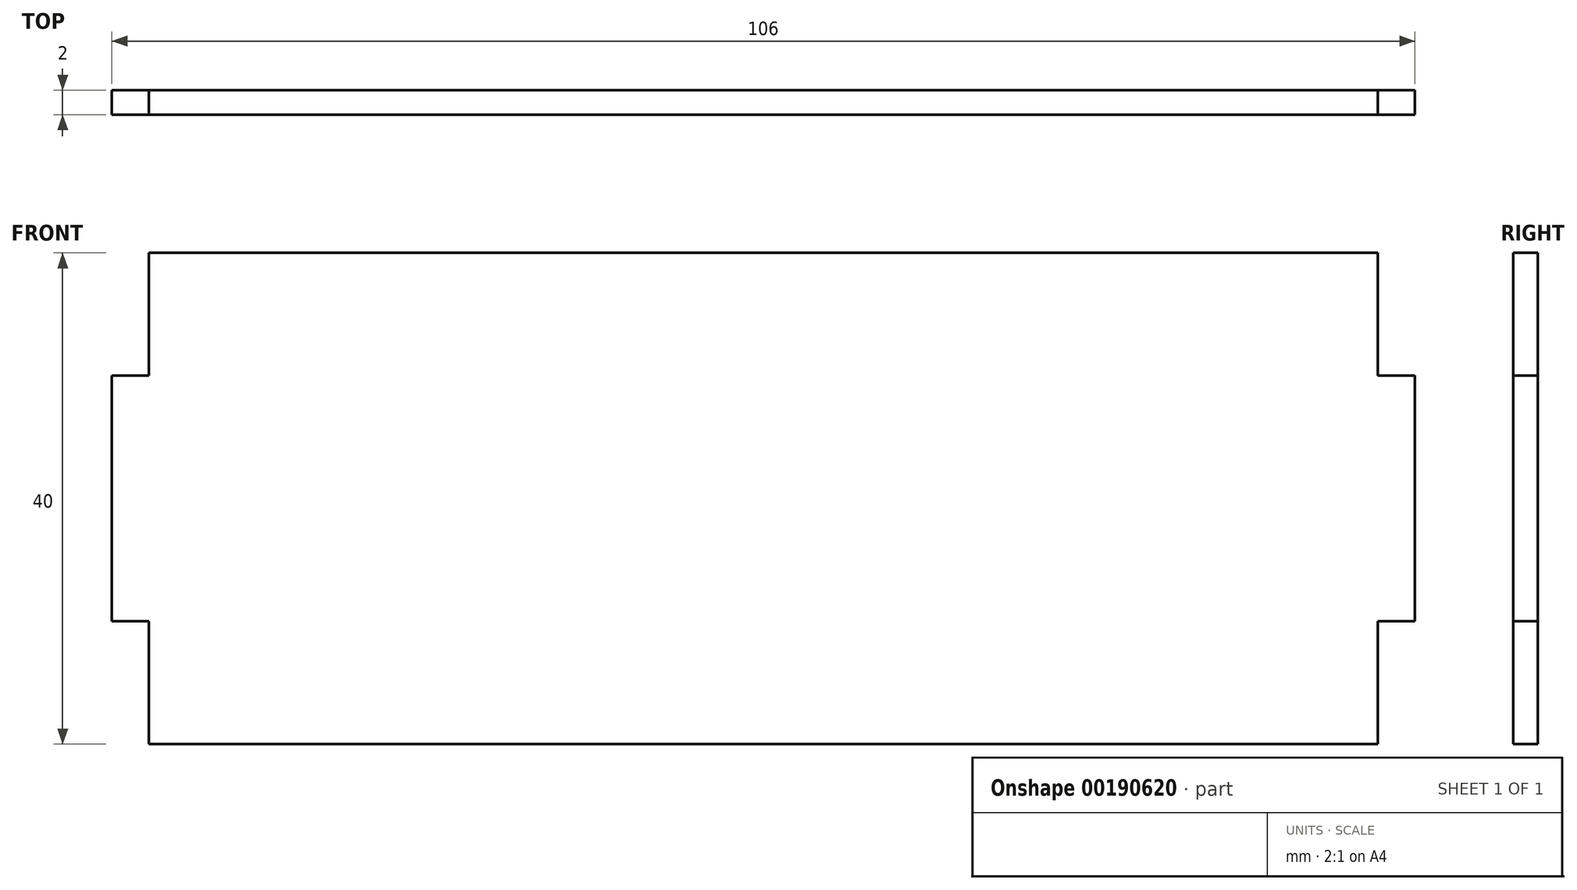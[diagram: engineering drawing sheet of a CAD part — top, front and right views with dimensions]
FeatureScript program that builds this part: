
annotation { "Feature Type Name" : "Feature", "Feature Type Description" : "" }
export const myFeature = defineFeature(function(context is Context, id is Id, definition is map)
    precondition{}
    {
        {
            var Q0;
            Q0=qCreatedBy(makeId("Front.planeOp"),FACE);
            var sketch = newSketch(context, id + "F0", { "sketchPlane" : qUnion([Q0])});
            skLineSegment(sketch, "E0.bottom", {"start": v(50, -20) * mm, "end": v(-50, -20) * mm});
            skLineSegment(sketch, "E0.top", {"start": v(50, 20) * mm, "end": v(-50, 20) * mm});
            skLineSegment(sketch, "E0.left", {"start": v(50, -20) * mm, "end": v(50, -10) * mm});
            skPoint(sketch, "E0.middle", {"position": v(0, 0) * mm});
            skLineSegment(sketch, "E1.bottom", {"start": v(50, -10) * mm, "end": v(53, -10) * mm});
            skLineSegment(sketch, "E1.top", {"start": v(50, 10) * mm, "end": v(53, 10) * mm});
            skLineSegment(sketch, "E1.right", {"start": v(53, -10) * mm, "end": v(53, 10) * mm});
            skLineSegment(sketch, "E2", {"start": v(0, 20) * mm, "end": v(0, -20) * mm, "construction": true});
            skLineSegment(sketch, "E3.trimOffspring", {"start": v(50, 10) * mm, "end": v(50, 20) * mm});
            skLineSegment(sketch, "E4.MirrorCS", {"start": v(-50, 10) * mm, "end": v(-50, 20) * mm});
            skLineSegment(sketch, "E5.MirrorCS", {"start": v(-50, 10) * mm, "end": v(-53, 10) * mm});
            skLineSegment(sketch, "E6.MirrorCS", {"start": v(-53, -10) * mm, "end": v(-53, 10) * mm});
            skLineSegment(sketch, "E7.MirrorCS", {"start": v(-50, -10) * mm, "end": v(-53, -10) * mm});
            skLineSegment(sketch, "E8.MirrorCS", {"start": v(-50, -20) * mm, "end": v(-50, -10) * mm});
            skPoint(sketch, "E9.MirrorCS.end.orphan", {"position": v(-50, 10) * mm});
            skPoint(sketch, "E9.MirrorCS.start.orphan", {"position": v(-50, -10) * mm});
            skSolve(sketch);
        }
        {
            var Q0;
            Q0=makeQuery(id+"F0.imprint","IMPRINT",FACE,{"disambiguationData":[TD([[makeQuery(id+"F0.imprint","IMPRINT",EDGE,{"derivedFrom":sQuery(id+"F0.wireOp",EDGE,"E0.bottom")}),-1.0]])]});
            extrude(context, id + "F1", {"entities" : qUnion([Q0]), "depth" : 2 * mm});
        }
    });
